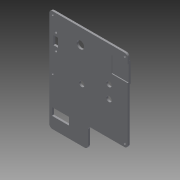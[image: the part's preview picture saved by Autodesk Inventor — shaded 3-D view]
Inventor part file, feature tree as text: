
AUTODESK INVENTOR PART (.ipt)
format: ipt  version: 2014 (Build 180170000, 170)  size: 548,864 bytes
history: native  units: mm
features: extrude x5, sketch x5, fillet x2
ambient origin geometry x8: Origin, YZ Plane, XZ Plane, XY Plane, X Axis, Y Axis, Z Axis, Center Point
bodies: Body1 (feature_tree)
feature tree (12):
  extrude  "押し出し4"  Depth=73.0mm
  extrude  "押し出し5"  Depth=76.0mm
  extrude  "押し出し6"  Depth=95.0mm
  fillet  "フィレット3"  Radius=36.0mm
  fillet  "フィレット4"  [1 undecoded]
  extrude  "押し出し7"  Depth=15.0mm
  extrude  "押し出し8"  Depth=8.0mm
  sketch  "スケッチ5"
  sketch  "スケッチ6"
  sketch  "スケッチ7"
  sketch  "スケッチ8"
  sketch  "スケッチ9"
note: 1 required parameter value undecoded (feature->parameter linkage not recoverable at this tier; creation-order binding heuristic only, values carry confidence <= 0.55)
